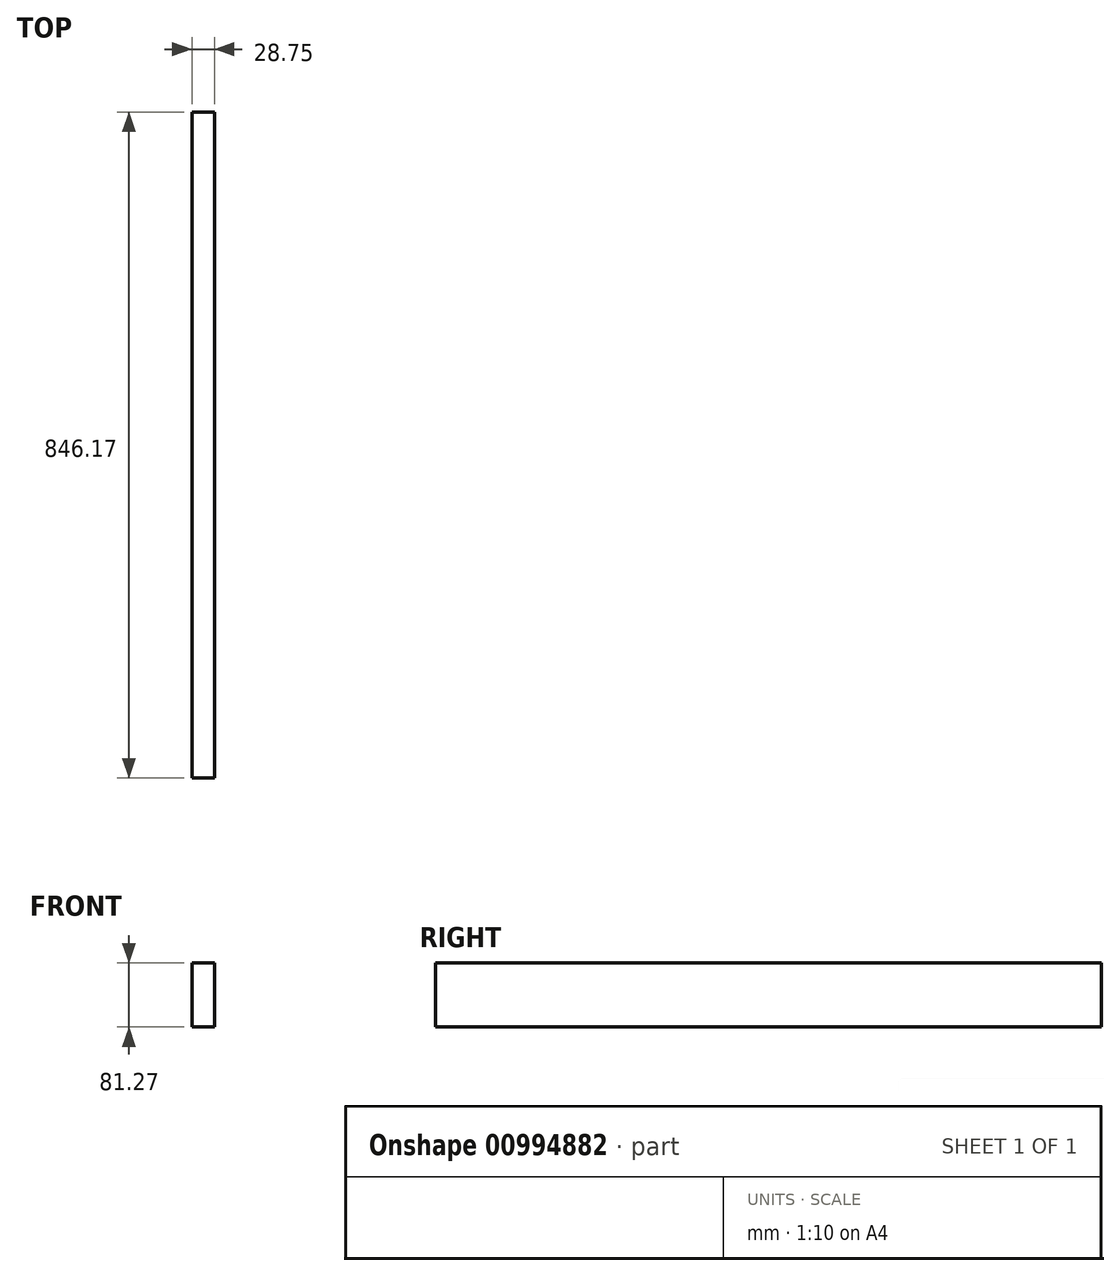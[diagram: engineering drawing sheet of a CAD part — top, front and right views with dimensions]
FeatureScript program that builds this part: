
annotation { "Feature Type Name" : "Feature", "Feature Type Description" : "" }
export const myFeature = defineFeature(function(context is Context, id is Id, definition is map)
    precondition{}
    {
        {
            var Q0;
            Q0=qCreatedBy(makeId("Front.planeOp"),FACE);
            var sketch = newSketch(context, id + "F0", { "sketchPlane" : qUnion([Q0])});
            skLineSegment(sketch, "E0.bottom", {"start": v(-61.42, -69.27) * mm, "end": v(-32.67, -69.27) * mm});
            skLineSegment(sketch, "E0.top", {"start": v(-61.42, 12) * mm, "end": v(-32.67, 12) * mm});
            skLineSegment(sketch, "E0.left", {"start": v(-61.42, -69.27) * mm, "end": v(-61.42, 12) * mm});
            skLineSegment(sketch, "E0.right", {"start": v(-32.67, -69.27) * mm, "end": v(-32.67, 12) * mm});
            skSolve(sketch);
        }
        {
            var Q0;
            Q0=makeQuery(id+"F0.imprint","IMPRINT",FACE,{"disambiguationData":[TD([[makeQuery(id+"F0.imprint","IMPRINT",EDGE,{"derivedFrom":sQuery(id+"F0.wireOp",EDGE,"E0.bottom")}),1.0]])]});
            var Q1;
            Q1 = qBodyType(qCreatedBy(id + "F2" ,EDGE), BodyType.WIRE);
            var Q2;
            Q2 = qBodyType(qCreatedBy(id + "F0" ,EDGE), BodyType.WIRE);
            extrude(context, id + "F1", {"entities" : qUnion([Q0]), "surfaceEntities" : qUnion([Q1, Q2]), "oppositeDirection" : true, "depth" : 846.17 * mm, "offsetDistance" : 25.4 * mm});
        }
    });
